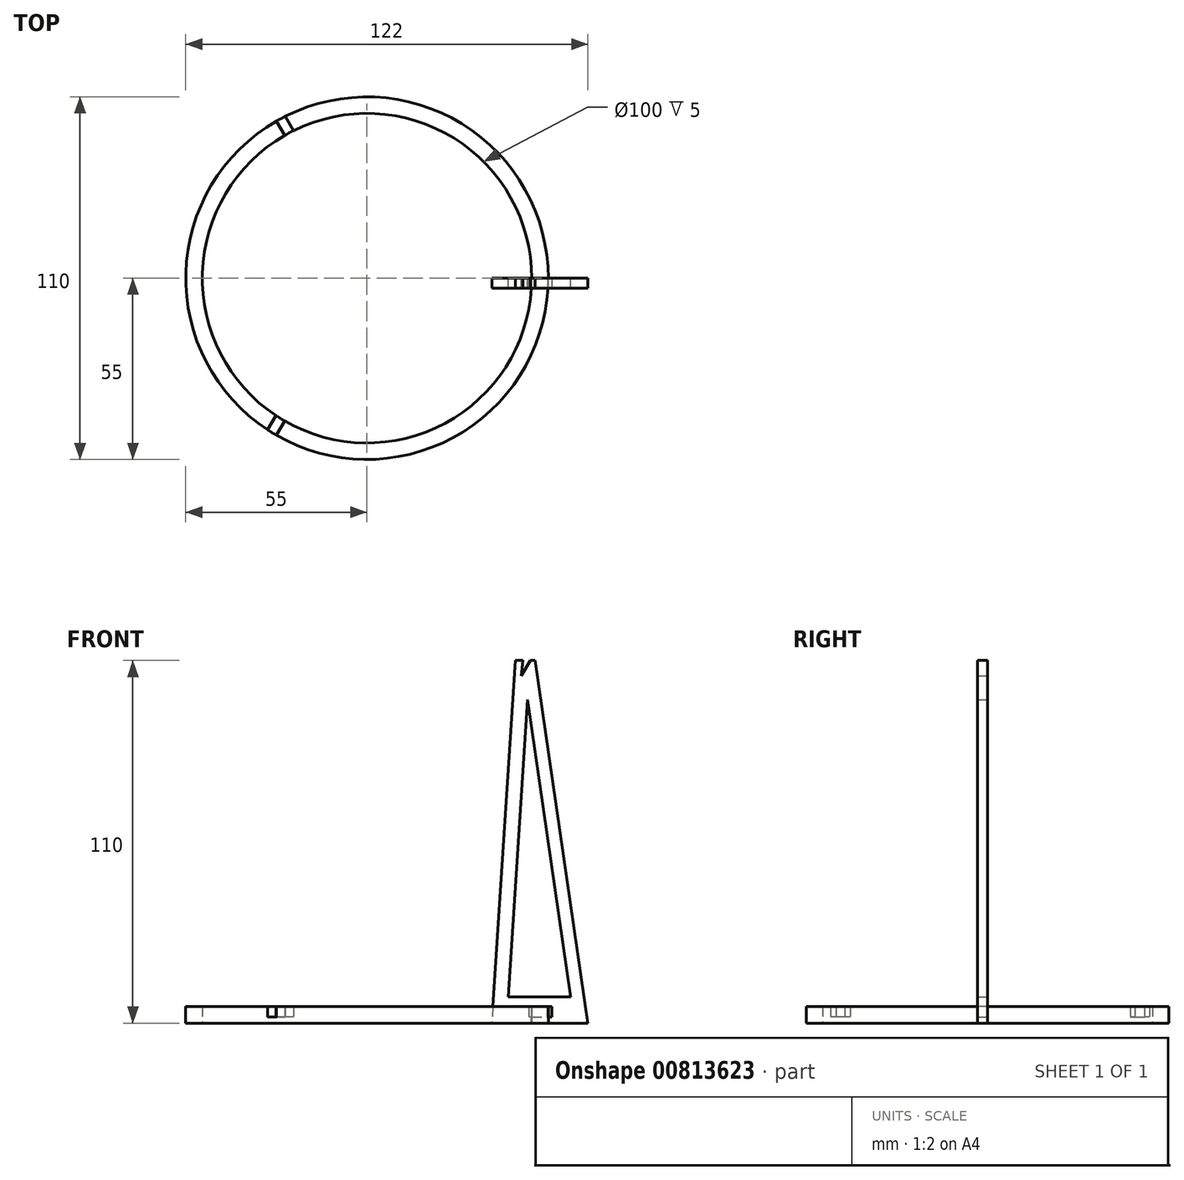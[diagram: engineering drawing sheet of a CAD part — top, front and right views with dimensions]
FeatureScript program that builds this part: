
annotation { "Feature Type Name" : "Feature", "Feature Type Description" : "" }
export const myFeature = defineFeature(function(context is Context, id is Id, definition is map)
    precondition{}
    {
        {
            var Q0;
            Q0=qCreatedBy(makeId("Top.planeOp"),FACE);
            var sketch = newSketch(context, id + "F0", { "sketchPlane" : qUnion([Q0])});
            skCircle(sketch, "E0", {"center": v(0, 0) * mm, "radius": 45 * mm, "construction": true});
            skSolve(sketch);
        }
        {
            var Q0;
            Q0=qCreatedBy(makeId("Front.planeOp"),FACE);
            var sketch = newSketch(context, id + "F1", { "sketchPlane" : qUnion([Q0])});
            skLineSegment(sketch, "E1", {"start": v(0, 0) * mm, "end": v(0, 110) * mm, "construction": true});
            skSolve(sketch);
        }
        {
            var Q0;
            Q0=qCreatedBy(makeId("Top.planeOp"),FACE);
            var Q1;
            Q1=sQuery(id+"F1.wireOp",VERTEX,"E1.end");
            cPlane(context, id + "F2", {"entities" : qUnion([Q0, Q1]), "cplaneType" : CPlaneType.PLANE_POINT, "offset" : 25 * mm, "width" : 150 * mm, "height" : 150 * mm});
        }
        {
            var Q0;
            Q0=qCreatedBy(id+"F2.planeOp",FACE);
            var sketch = newSketch(context, id + "F3", { "sketchPlane" : qUnion([Q0])});
            skCircle(sketch, "E2", {"center": v(0, 0) * mm, "radius": 45 * mm, "construction": true});
            skSolve(sketch);
        }
        {
            var Q0;
            Q0=qCreatedBy(makeId("Front.planeOp"),FACE);
            var sketch = newSketch(context, id + "F4", { "sketchPlane" : qUnion([Q0])});
            skLineSegment(sketch, "E3.0", {"start": v(-45, 110) * mm, "end": v(45, 110) * mm, "construction": true});
            skLineSegment(sketch, "E4", {"start": v(45, 110) * mm, "end": v(37.88, 0) * mm});
            skLineSegment(sketch, "E5", {"start": v(37.88, 0) * mm, "end": v(49.8, 0) * mm});
            skLineSegment(sketch, "E6", {"start": v(67, 0) * mm, "end": v(51, 110) * mm});
            skLineSegment(sketch, "E7", {"start": v(51, 110) * mm, "end": v(49.62, 110) * mm});
            skLineSegment(sketch, "E8.0", {"start": v(-45, 0) * mm, "end": v(45, 0) * mm, "construction": true});
            skLineSegment(sketch, "E9", {"start": v(49.62, 110) * mm, "end": v(46.82, 105.4) * mm});
            skLineSegment(sketch, "E10", {"start": v(46.82, 105.4) * mm, "end": v(47.27, 110) * mm});
            skLineSegment(sketch, "E11.trimOffspring", {"start": v(47.27, 110) * mm, "end": v(45, 110) * mm});
            skLineSegment(sketch, "E12", {"start": v(42.89, 8) * mm, "end": v(48.72, 98.15) * mm});
            skLineSegment(sketch, "E13", {"start": v(48.72, 98.15) * mm, "end": v(61.84, 8) * mm});
            skLineSegment(sketch, "E14", {"start": v(61.84, 8) * mm, "end": v(42.89, 8) * mm});
            skLineSegment(sketch, "E15.top", {"start": v(49.8, 2) * mm, "end": v(55, 2) * mm});
            skLineSegment(sketch, "E15.left", {"start": v(49.8, 0) * mm, "end": v(49.8, 2) * mm});
            skLineSegment(sketch, "E15.right", {"start": v(55, 0) * mm, "end": v(55, 2) * mm});
            skLineSegment(sketch, "E16.trimOffspring", {"start": v(55, 0) * mm, "end": v(67, 0) * mm});
            skSolve(sketch);
        }
        {
            var Q0;
            Q0=makeQuery(id+"F4.imprint","IMPRINT",FACE,{"disambiguationData":[TD([[makeQuery(id+"F4.imprint","IMPRINT",EDGE,{"derivedFrom":sQuery(id+"F4.wireOp",EDGE,"E4")}),1.0]])]});
            extrude(context, id + "F5", {"entities" : qUnion([Q0]), "depth" : 3 * mm, "offsetDistance" : 25 * mm});
        }
        {
            var Q0;
            Q0=qCreatedBy(makeId("Top.planeOp"),FACE);
            var sketch = newSketch(context, id + "F6", { "sketchPlane" : qUnion([Q0])});
            skCircle(sketch, "E17", {"center": v(0, 0) * mm, "radius": 50 * mm});
            skCircle(sketch, "E18.0", {"center": v(0, 0) * mm, "radius": 45 * mm, "construction": true});
            skCircle(sketch, "E19.0", {"center": v(0, 0) * mm, "radius": 55 * mm});
            skSolve(sketch);
        }
        {
            var Q0;
            Q0 = qSketchRegion(id + "F6", true);
            extrude(context, id + "F7", {"entities" : qUnion([Q0]), "depth" : 5 * mm, "offsetDistance" : 25 * mm});
        }
        {
            var Q0;
            Q0=makeQuery(id+"F7.opExtrude","CAP_FACE",FACE,{"disambiguationData":[OSD([sQuery(id+"F6.wireOp",EDGE,"E17"),sQuery(id+"F6.wireOp",EDGE,"E19.0")])],"isStart":false});
            var sketch = newSketch(context, id + "F8", { "sketchPlane" : qUnion([Q0])});
            skLineSegment(sketch, "E20.bottom", {"start": v(49.06, 0) * mm, "end": v(56.04, 0) * mm});
            skLineSegment(sketch, "E20.top", {"start": v(49.06, -3.1) * mm, "end": v(56.04, -3.1) * mm});
            skLineSegment(sketch, "E20.left", {"start": v(49.06, 0) * mm, "end": v(49.06, -3.1) * mm});
            skLineSegment(sketch, "E20.right", {"start": v(56.04, 0) * mm, "end": v(56.04, -3.1) * mm});
            skLineSegment(sketch, "E21.1.0", {"start": v(-24.53, 42.49) * mm, "end": v(-28.02, 48.53) * mm});
            skLineSegment(sketch, "E21.1.1", {"start": v(-21.84, 44.04) * mm, "end": v(-25.33, 50.08) * mm});
            skLineSegment(sketch, "E21.1.2", {"start": v(-24.53, 42.49) * mm, "end": v(-21.84, 44.04) * mm});
            skLineSegment(sketch, "E21.1.3", {"start": v(-28.02, 48.53) * mm, "end": v(-25.33, 50.08) * mm});
            skLineSegment(sketch, "E21.2.0", {"start": v(-24.53, -42.49) * mm, "end": v(-28.02, -48.53) * mm});
            skLineSegment(sketch, "E21.2.1", {"start": v(-27.21, -40.94) * mm, "end": v(-30.7, -46.98) * mm});
            skLineSegment(sketch, "E21.2.2", {"start": v(-24.53, -42.49) * mm, "end": v(-27.21, -40.94) * mm});
            skLineSegment(sketch, "E21.2.3", {"start": v(-28.02, -48.53) * mm, "end": v(-30.7, -46.98) * mm});
            skPoint(sketch, "E21.center", {"position": v(0, 0) * mm});
            skSolve(sketch);
        }
        {
            var Q0;
            Q0 = qSketchRegion(id + "F8", true);
            extrude(context, id + "F9", {"entities" : qUnion([Q0]), "operationType" : NewBodyOperationType.REMOVE, "oppositeDirection" : true, "depth" : 3.2 * mm, "offsetDistance" : 25 * mm});
        }
    });
